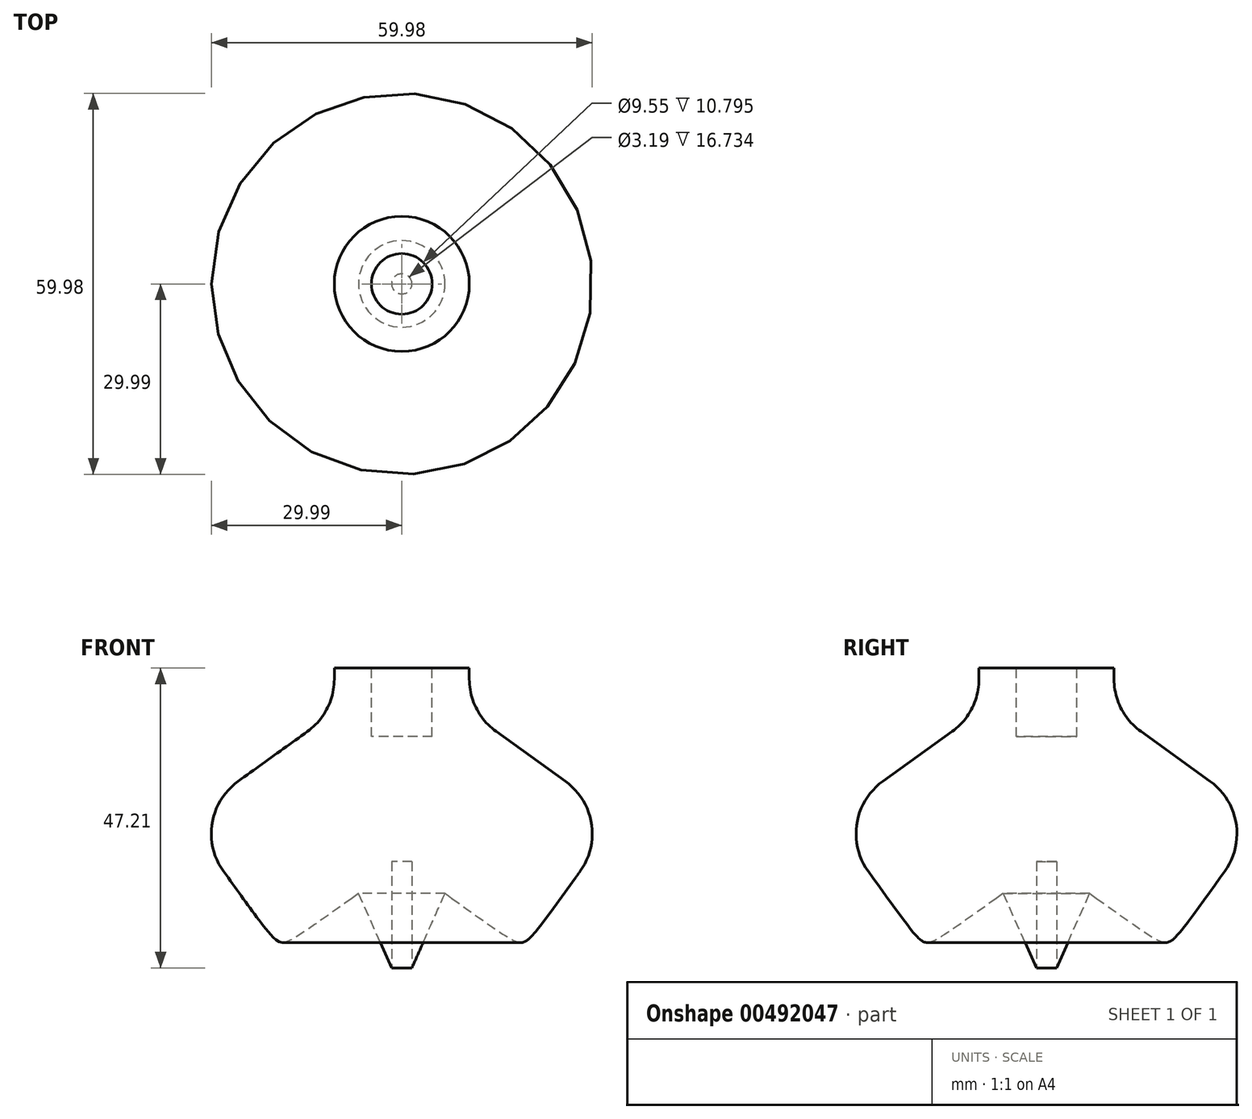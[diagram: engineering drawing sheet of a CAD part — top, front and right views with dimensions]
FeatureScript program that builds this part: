
annotation { "Feature Type Name" : "Feature", "Feature Type Description" : "" }
export const myFeature = defineFeature(function(context is Context, id is Id, definition is map)
    precondition{}
    {
        {
            var Q0;
            Q0=qCreatedBy(makeId("Front.planeOp"),FACE);
            var sketch = newSketch(context, id + "F0", { "sketchPlane" : qUnion([Q0])});
            skLineSegment(sketch, "E0", {"start": v(0, 0) * mm, "end": v(6.8, 15.32) * mm});
            skLineSegment(sketch, "E1", {"start": v(6.8, 15.32) * mm, "end": v(19.18, 6.42) * mm});
            skLineSegment(sketch, "E2", {"start": v(19.18, 6.42) * mm, "end": v(34, 27.05) * mm});
            skLineSegment(sketch, "E3", {"start": v(34, 27.05) * mm, "end": v(10.63, 43.85) * mm});
            skLineSegment(sketch, "E4", {"start": v(10.63, 43.85) * mm, "end": v(10.63, 50.8) * mm});
            skLineSegment(sketch, "E5", {"start": v(10.63, 50.8) * mm, "end": v(0, 50.8) * mm});
            skLineSegment(sketch, "E6", {"start": v(0, 50.8) * mm, "end": v(0, 0) * mm});
            skSolve(sketch);
        }
        {
            var Q0;
            Q0=makeQuery(id+"F0.imprint","IMPRINT",FACE,{"disambiguationData":[TD([[makeQuery(id+"F0.imprint","IMPRINT",EDGE,{"derivedFrom":sQuery(id+"F0.wireOp",EDGE,"E0")}),1.0]])]});
            var Q1;
            Q1=sQuery(id+"F0.wireOp",EDGE,"E6");
            revolve(context, id + "F1", {"entities" : qUnion([Q0]), "axis" : qUnion([Q1]), "revolveType" : RevolveType.FULL});
        }
        {
            var Q0;
            Q0=makeQuery(id+"F1.opRevolve","SWEPT_EDGE",EDGE,{"disambiguationData":[OSD([sQuery(id+"F0.wireOp",EDGE,"E3"),sQuery(id+"F0.wireOp",EDGE,"E4")])]});
            fillet(context, id + "F2", {"entities" : qUnion([Q0]), "radius" : 10.16 * mm, "tangentPropagation" : true, "allowEdgeOverflow" : false});
        }
        {
            var Q0;
            Q0=makeQuery(id+"F1.opRevolve","SWEPT_FACE",FACE,{"disambiguationData":[OSD([sQuery(id+"F0.wireOp",EDGE,"E3")])]});
            fillet(context, id + "F3", {"entities" : qUnion([Q0]), "radius" : 10.16 * mm, "tangentPropagation" : true, "allowEdgeOverflow" : false});
        }
        {
            var Q0;
            Q0=makeQuery(id+"F1.opRevolve","SWEPT_FACE",FACE,{"disambiguationData":[OSD([sQuery(id+"F0.wireOp",EDGE,"E2")])]});
            fillet(context, id + "F4", {"entities" : qUnion([Q0]), "radius" : 13.97 * mm, "tangentPropagation" : true, "rho" : 0.88, "crossSection" : FilletCrossSection.CONIC, "allowEdgeOverflow" : false});
        }
        {
            var Q0;
            Q0=makeQuery(id+"F1.opRevolve","SWEPT_FACE",FACE,{"disambiguationData":[OSD([sQuery(id+"F0.wireOp",EDGE,"E5")])]});
            var sketch = newSketch(context, id + "F5", { "sketchPlane" : qUnion([Q0])});
            skCircle(sketch, "E7", {"center": v(0, 0) * mm, "radius": 4.78 * mm});
            skSolve(sketch);
        }
        {
            var Q0;
            Q0=makeQuery(id+"F5.imprint","IMPRINT",FACE,{"disambiguationData":[TD([[makeQuery(id+"F5.imprint","IMPRINT",EDGE,{"derivedFrom":sQuery(id+"F5.wireOp",EDGE,"E7")}),1.0]])]});
            var Q1;
            Q1=sQuery(id+"F5.wireOp",EDGE,"E7");
            extrude(context, id + "F6", {"entities" : qUnion([Q0]), "operationType" : NewBodyOperationType.REMOVE, "surfaceEntities" : qUnion([Q1]), "oppositeDirection" : true, "depth" : 10.8 * mm});
        }
        {
            var Q0;
            Q0=qCreatedBy(makeId("Top.planeOp"),FACE);
            var sketch = newSketch(context, id + "F7", { "sketchPlane" : qUnion([Q0])});
            skCircle(sketch, "E8", {"center": v(0, 0) * mm, "radius": 1.6 * mm});
            skSolve(sketch);
        }
        {
            var Q0;
            Q0=makeQuery(id+"F7.imprint","IMPRINT",FACE,{"disambiguationData":[TD([[makeQuery(id+"F7.imprint","IMPRINT",EDGE,{"derivedFrom":sQuery(id+"F7.wireOp",EDGE,"E8")}),1.0]])]});
            var Q1;
            Q1=sQuery(id+"F7.wireOp",EDGE,"E8");
            extrude(context, id + "F8", {"entities" : qUnion([Q0]), "operationType" : NewBodyOperationType.REMOVE, "surfaceEntities" : qUnion([Q1]), "depth" : 20.32 * mm});
        }
    });
